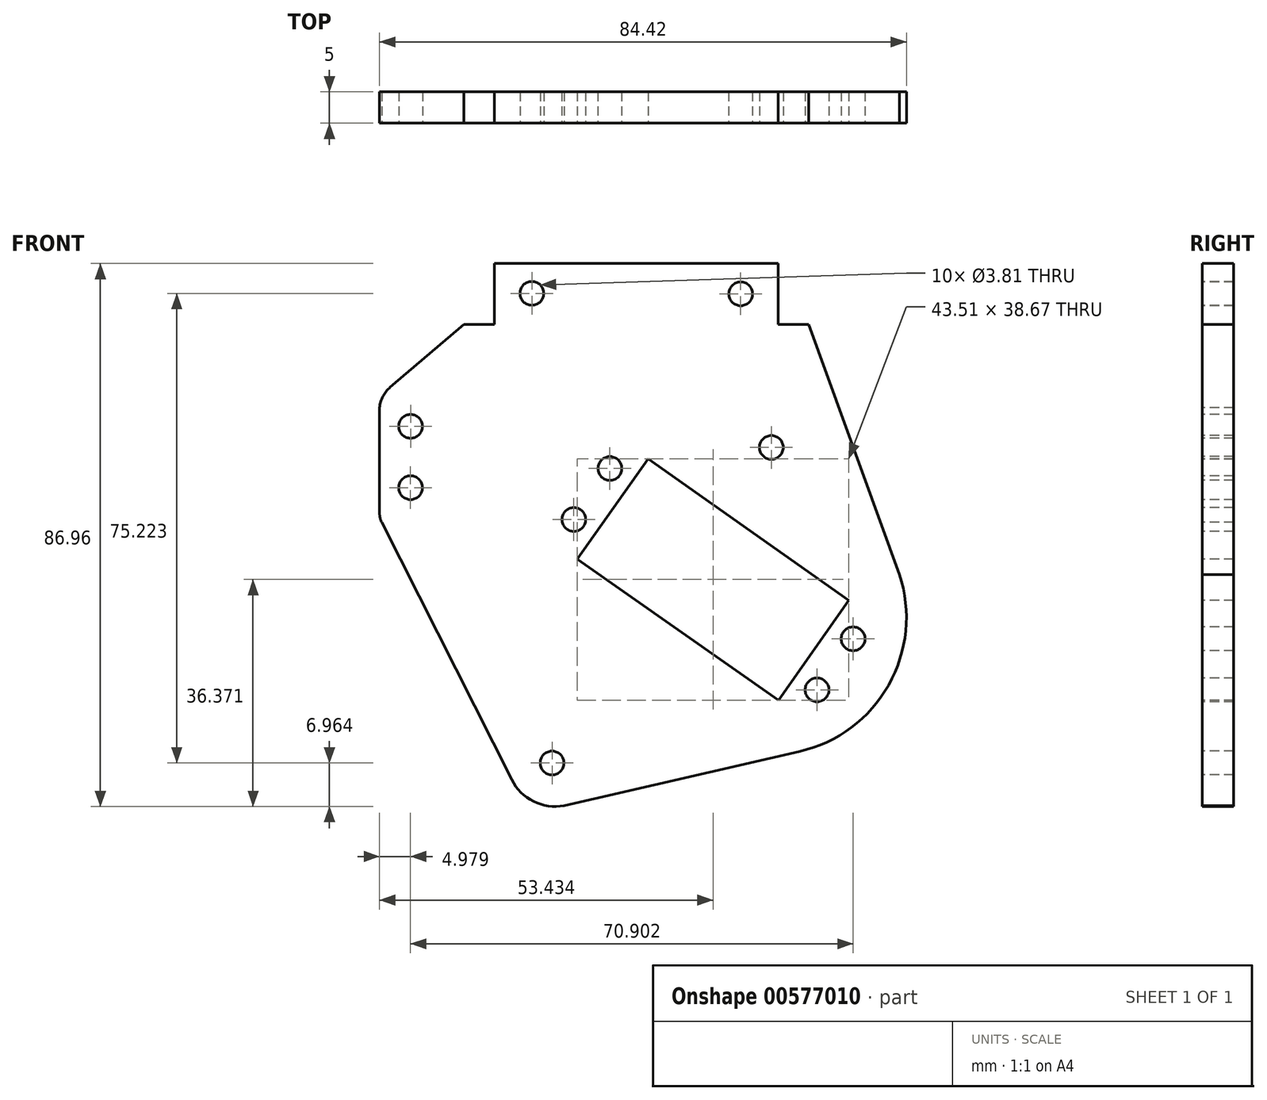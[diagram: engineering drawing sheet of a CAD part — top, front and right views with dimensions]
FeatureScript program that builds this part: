
annotation { "Feature Type Name" : "Feature", "Feature Type Description" : "" }
export const myFeature = defineFeature(function(context is Context, id is Id, definition is map)
    precondition{}
    {
        {
            var Q0;
            Q0=qCreatedBy(makeId("Front.planeOp"),FACE);
            var sketch = newSketch(context, id + "F0", { "sketchPlane" : qUnion([Q0])});
            skLineSegment(sketch, "E0", {"start": v(19.64, 89.45) * mm, "end": v(19.64, 79.72) * mm});
            skLineSegment(sketch, "E1", {"start": v(19.64, 79.72) * mm, "end": v(14.76, 79.72) * mm});
            skLineSegment(sketch, "E2", {"start": v(14.76, 79.72) * mm, "end": v(2.94, 69.65) * mm});
            skLineSegment(sketch, "E3", {"start": v(19.64, 89.45) * mm, "end": v(65.11, 89.45) * mm});
            skLineSegment(sketch, "E4", {"start": v(65.11, 89.45) * mm, "end": v(65.11, 79.7) * mm});
            skLineSegment(sketch, "E5", {"start": v(65.11, 79.7) * mm, "end": v(69.98, 79.7) * mm});
            skLineSegment(sketch, "E6", {"start": v(69.98, 79.7) * mm, "end": v(84.53, 39.63) * mm});
            skLineSegment(sketch, "E7", {"start": v(30.78, 2.62) * mm, "end": v(68.54, 11.3) * mm});
            skLineSegment(sketch, "E8", {"start": v(1.21, 66.37) * mm, "end": v(1.21, 49.52) * mm});
            skLineSegment(sketch, "E9", {"start": v(1.56, 48) * mm, "end": v(22.4, 6.78) * mm});
            skArc(sketch, "E10", {"start": v(2.94, 69.65) * mm, "mid": v(1.76, 68.18) * mm, "end": v(1.21, 66.37) * mm});
            skArc(sketch, "E11", {"start": v(1.21, 49.52) * mm, "mid": v(1.3, 48.74) * mm, "end": v(1.56, 48) * mm});
            skArc(sketch, "E12", {"start": v(22.4, 6.78) * mm, "mid": v(25.9, 3.3) * mm, "end": v(30.78, 2.62) * mm});
            skArc(sketch, "E13", {"start": v(68.54, 11.3) * mm, "mid": v(82.78, 21.95) * mm, "end": v(84.53, 39.63) * mm});
            skLineSegment(sketch, "E14", {"start": v(32.89, 42.1) * mm, "end": v(44.27, 58.2) * mm});
            skLineSegment(sketch, "E15", {"start": v(44.27, 58.2) * mm, "end": v(76.4, 35.49) * mm});
            skLineSegment(sketch, "E16", {"start": v(76.4, 35.49) * mm, "end": v(65.11, 19.52) * mm});
            skLineSegment(sketch, "E17", {"start": v(65.11, 19.52) * mm, "end": v(32.89, 42.1) * mm});
            skCircle(sketch, "E18", {"center": v(38.12, 56.63) * mm, "radius": 1.9 * mm});
            skPoint(sketch, "E18.first.point", {"position": v(38.07, 58.53) * mm});
            skPoint(sketch, "E18.second.point", {"position": v(40.02, 56.8) * mm});
            skPoint(sketch, "E18.third.point", {"position": v(36.96, 55.12) * mm});
            skCircle(sketch, "E19", {"center": v(32.35, 48.46) * mm, "radius": 1.9 * mm});
            skPoint(sketch, "E19.first.point", {"position": v(32.68, 46.58) * mm});
            skPoint(sketch, "E19.second.point", {"position": v(32.7, 50.33) * mm});
            skPoint(sketch, "E19.third.point", {"position": v(30.65, 49.32) * mm});
            skCircle(sketch, "E20", {"center": v(6.2, 63.38) * mm, "radius": 1.9 * mm});
            skPoint(sketch, "E20.first.point", {"position": v(6.19, 65.29) * mm});
            skPoint(sketch, "E20.second.point", {"position": v(8.1, 63.37) * mm});
            skPoint(sketch, "E20.third.point", {"position": v(5.37, 61.67) * mm});
            skCircle(sketch, "E21", {"center": v(6.19, 53.55) * mm, "radius": 1.9 * mm});
            skPoint(sketch, "E21.first.point", {"position": v(5.44, 55.3) * mm});
            skPoint(sketch, "E21.second.point", {"position": v(8.1, 53.49) * mm});
            skPoint(sketch, "E21.third.point", {"position": v(6.06, 51.65) * mm});
            skCircle(sketch, "E22", {"center": v(28.86, 9.45) * mm, "radius": 1.9 * mm});
            skCircle(sketch, "E23", {"center": v(71.31, 21.17) * mm, "radius": 1.9 * mm});
            skCircle(sketch, "E24", {"center": v(77.1, 29.34) * mm, "radius": 1.9 * mm});
            skCircle(sketch, "E25", {"center": v(63.99, 60) * mm, "radius": 1.9 * mm});
            skCircle(sketch, "E26", {"center": v(59.08, 84.6) * mm, "radius": 1.9 * mm});
            skCircle(sketch, "E27", {"center": v(25.62, 84.68) * mm, "radius": 1.9 * mm});
            skSolve(sketch);
        }
        {
            var Q0;
            Q0=makeQuery(id+"F0.imprint","IMPRINT",FACE,{"disambiguationData":[TD([[makeQuery(id+"F0.imprint","IMPRINT",EDGE,{"derivedFrom":sQuery(id+"F0.wireOp",EDGE,"E0")}),1.0]])]});
            extrude(context, id + "F1", {"entities" : qUnion([Q0]), "oppositeDirection" : true, "depth" : 5 * mm, "offsetDistance" : 25.4 * mm});
        }
    });
